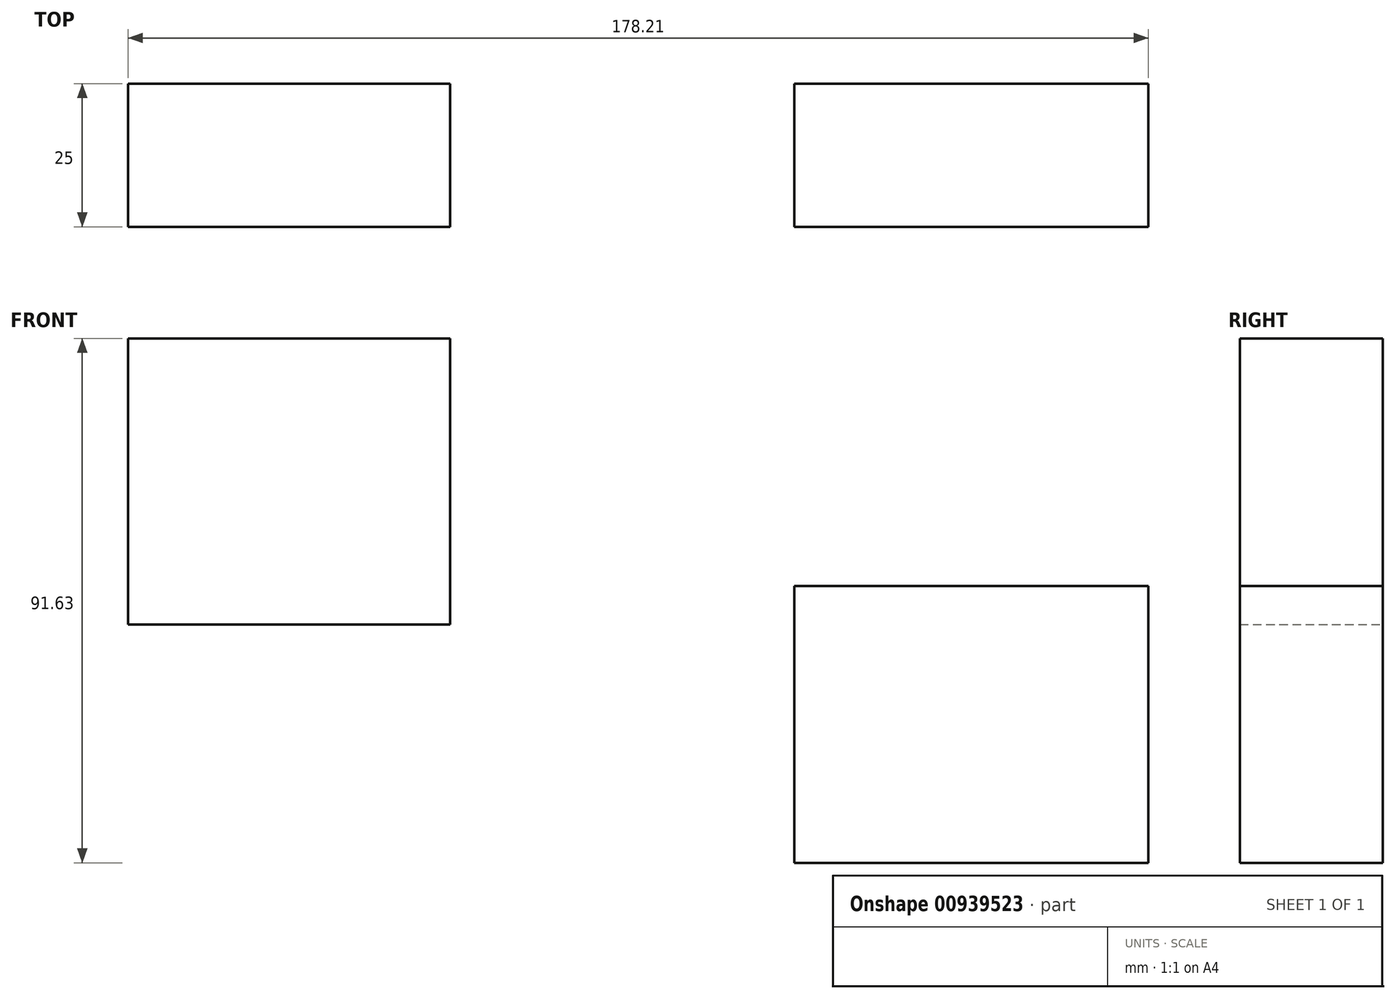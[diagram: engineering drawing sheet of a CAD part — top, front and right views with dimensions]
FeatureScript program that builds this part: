
annotation { "Feature Type Name" : "Feature", "Feature Type Description" : "" }
export const myFeature = defineFeature(function(context is Context, id is Id, definition is map)
    precondition{}
    {
        {
            var Q0;
            Q0=qCreatedBy(makeId("Front.planeOp"),FACE);
            var sketch = newSketch(context, id + "F0", { "sketchPlane" : qUnion([Q0])});
            skLineSegment(sketch, "E0.bottom", {"start": v(-113.7, 11.1) * mm, "end": v(-57.48, 11.1) * mm});
            skLineSegment(sketch, "E0.top", {"start": v(-113.7, 61.13) * mm, "end": v(-57.48, 61.13) * mm});
            skLineSegment(sketch, "E0.left", {"start": v(-113.7, 11.1) * mm, "end": v(-113.7, 61.13) * mm});
            skLineSegment(sketch, "E0.right", {"start": v(-57.48, 11.1) * mm, "end": v(-57.48, 61.13) * mm});
            skPoint(sketch, "E0.middle", {"position": v(-85.59, 36.12) * mm});
            skLineSegment(sketch, "E1.bottom", {"start": v(2.67, -30.5) * mm, "end": v(64.5, -30.5) * mm});
            skLineSegment(sketch, "E1.top", {"start": v(2.67, 17.85) * mm, "end": v(64.5, 17.85) * mm});
            skLineSegment(sketch, "E1.left", {"start": v(2.67, -30.5) * mm, "end": v(2.67, 17.85) * mm});
            skLineSegment(sketch, "E1.right", {"start": v(64.5, -30.5) * mm, "end": v(64.5, 17.85) * mm});
            skPoint(sketch, "E1.middle", {"position": v(33.59, -6.32) * mm});
            skSolve(sketch);
        }
        {
            var Q0;
            Q0=makeQuery(id+"F0.imprint","IMPRINT",FACE,{"disambiguationData":[TD([[makeQuery(id+"F0.imprint","IMPRINT",EDGE,{"derivedFrom":sQuery(id+"F0.wireOp",EDGE,"E1.bottom")}),1.0]])]});
            var Q1;
            Q1=makeQuery(id+"F0.imprint","IMPRINT",FACE,{"disambiguationData":[TD([[makeQuery(id+"F0.imprint","IMPRINT",EDGE,{"derivedFrom":sQuery(id+"F0.wireOp",EDGE,"E0.bottom")}),1.0]])]});
            extrude(context, id + "F1", {"entities" : qUnion([Q0, Q1]), "depth" : 25 * mm, "offsetDistance" : 25 * mm});
        }
    });
